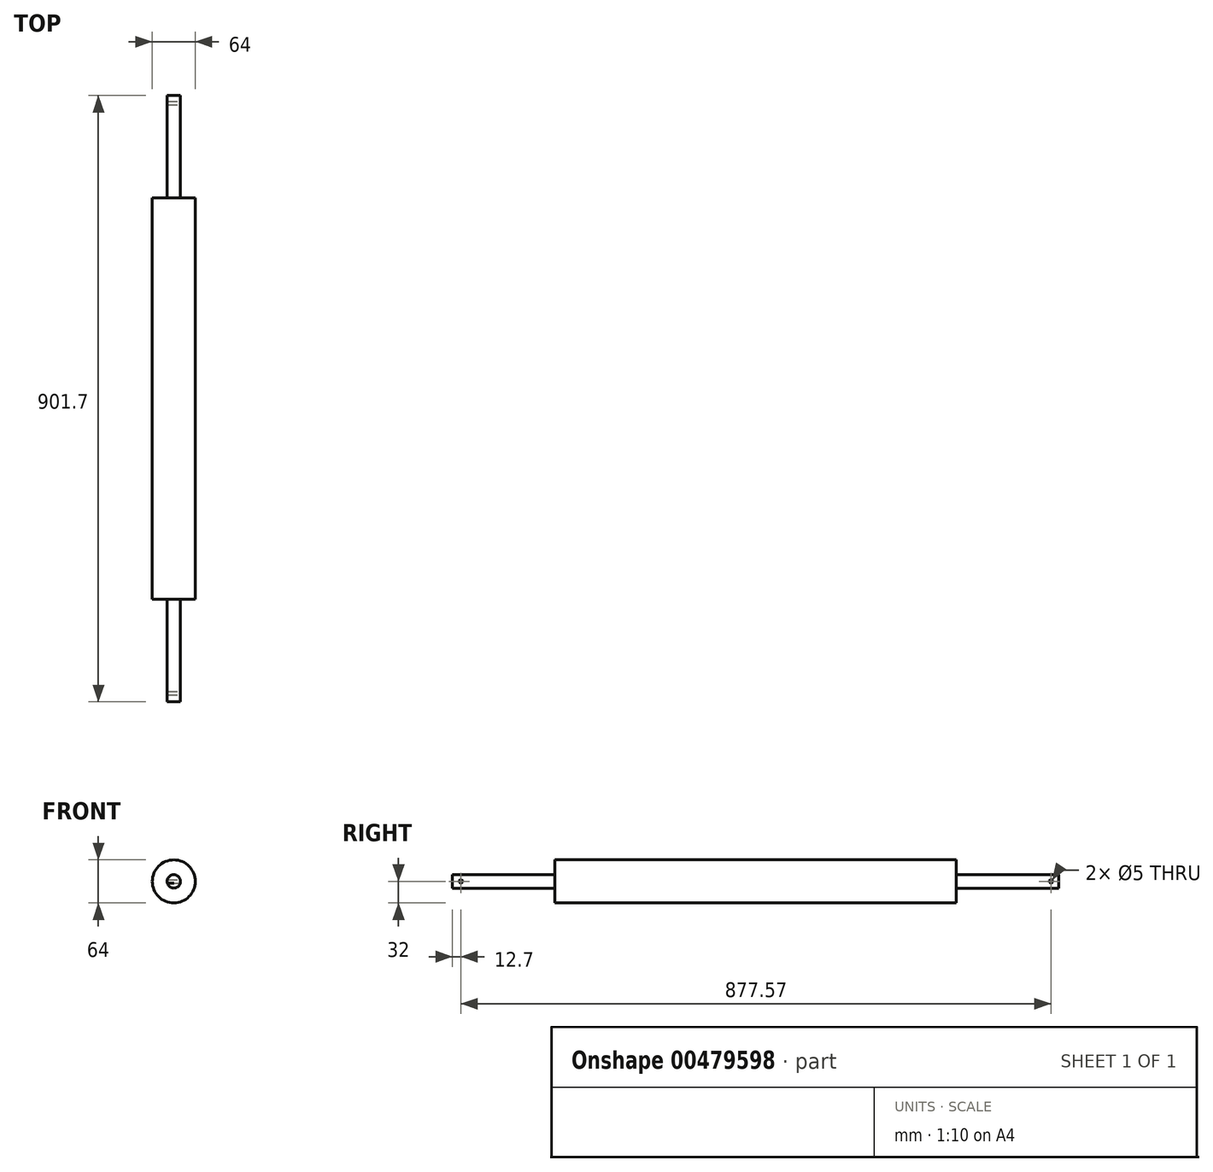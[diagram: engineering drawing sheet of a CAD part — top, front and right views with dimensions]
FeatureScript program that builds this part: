
annotation { "Feature Type Name" : "Feature", "Feature Type Description" : "" }
export const myFeature = defineFeature(function(context is Context, id is Id, definition is map)
    precondition{}
    {
        {
            var Q0;
            Q0=qCreatedBy(makeId("Front.planeOp"),FACE);
            var sketch = newSketch(context, id + "F0", { "sketchPlane" : qUnion([Q0])});
            skCircle(sketch, "E0", {"center": v(0, 0) * mm, "radius": 32 * mm});
            skCircle(sketch, "E1", {"center": v(0, 0) * mm, "radius": 10 * mm});
            skSolve(sketch);
        }
        {
            var Q0;
            Q0=qSketchRegion(id+"F0",true);
            var Q1;
            Q1=makeQuery(id+"F0.imprint","IMPRINT",FACE,{"disambiguationData":[TD([[makeQuery(id+"F0.imprint","IMPRINT",EDGE,{"derivedFrom":sQuery(id+"F0.wireOp",EDGE,"E1")}),1.0]])]});
            var Q2;
            Q2 = qSketchRegion(id + "F3", true);
            extrude(context, id + "F1", {"entities" : qUnion([Q0, Q1, Q2]), "oppositeDirection" : true, "depth" : 596.9 * mm});
        }
        {
            var Q0;
            Q0=makeQuery(id+"F0.imprint","IMPRINT",FACE,{"disambiguationData":[TD([[makeQuery(id+"F0.imprint","IMPRINT",EDGE,{"derivedFrom":sQuery(id+"F0.wireOp",EDGE,"E1")}),1.0]])]});
            extrude(context, id + "F2", {"entities" : qUnion([Q0]), "operationType" : NewBodyOperationType.ADD, "depth" : 152.4 * mm});
        }
        {
            var Q0;
            Q0=makeQuery(id+"F1.opExtrude","CAP_FACE",FACE,{"disambiguationData":[OSD([sQuery(id+"F0.wireOp",EDGE,"E0")])],"isStart":false});
            var sketch = newSketch(context, id + "F3", { "sketchPlane" : qUnion([Q0])});
            skCircle(sketch, "E2", {"center": v(0, 0) * mm, "radius": 10 * mm});
            skSolve(sketch);
        }
        {
            var Q0;
            Q0=qSketchRegion(id+"F3",true);
            extrude(context, id + "F4", {"entities" : qUnion([Q0]), "operationType" : NewBodyOperationType.ADD, "depth" : 152.4 * mm});
        }
        {
            var Q0;
            Q0=qCreatedBy(makeId("Right.planeOp"),FACE);
            var sketch = newSketch(context, id + "F5", { "sketchPlane" : qUnion([Q0])});
            skCircle(sketch, "E3", {"center": v(-139.7, 0) * mm, "radius": 2.5 * mm});
            skCircle(sketch, "E4", {"center": v(737.87, 0) * mm, "radius": 2.5 * mm});
            skSolve(sketch);
        }
        {
            var Q0;
            Q0=qSketchRegion(id+"F5",true);
            extrude(context, id + "F6", {"entities" : qUnion([Q0]), "operationType" : NewBodyOperationType.REMOVE, "endBound" : BoundingType.SYMMETRIC, "oppositeDirection" : true, "depth" : 127 * mm});
        }
    });
